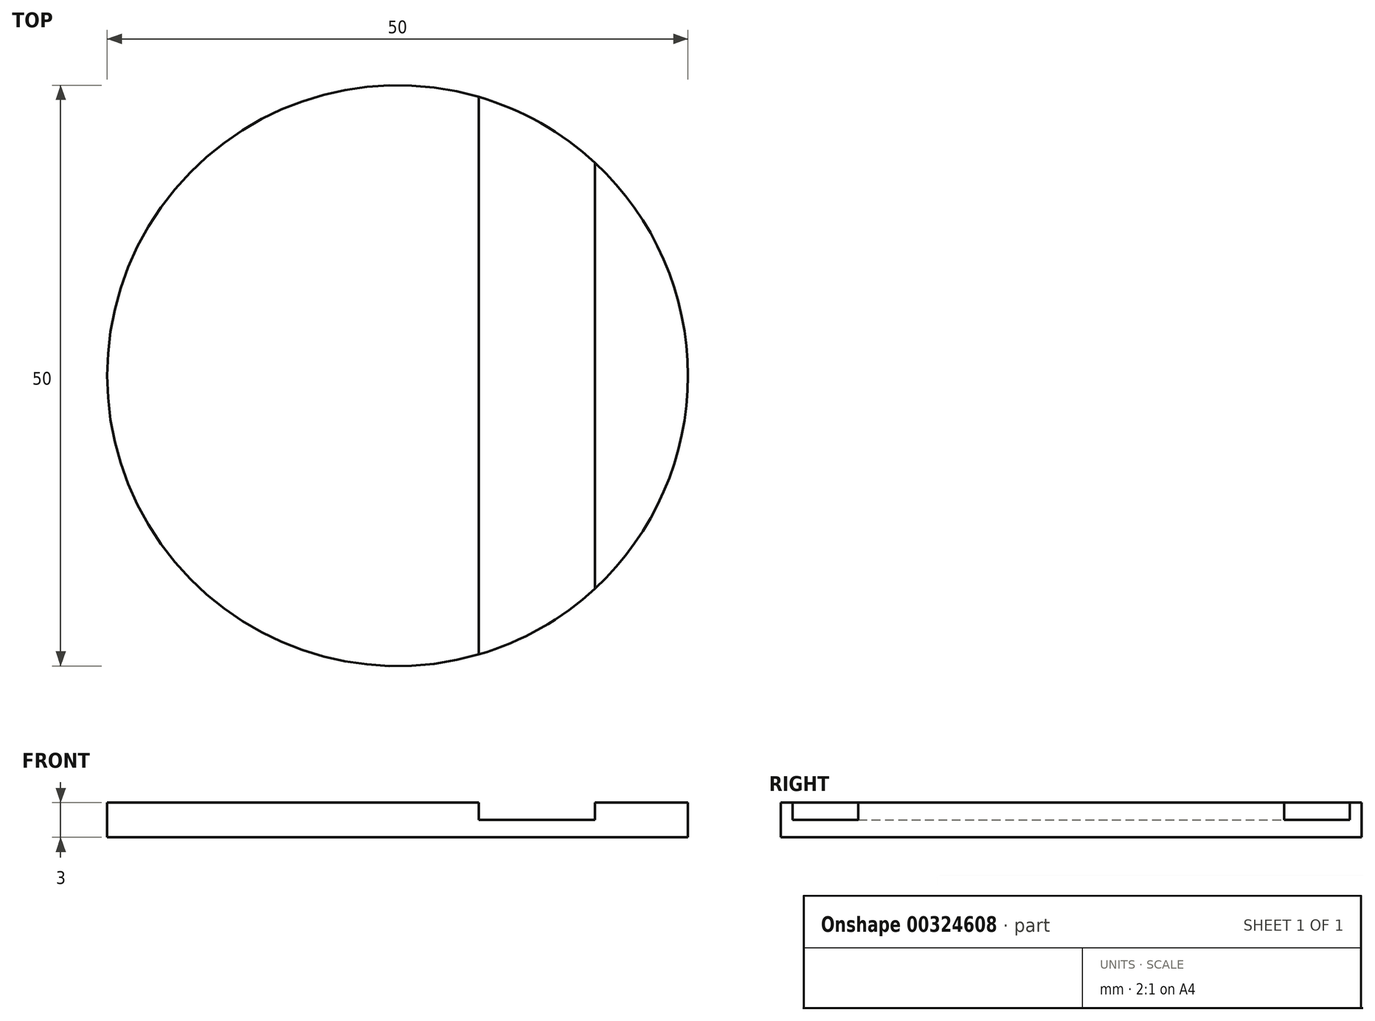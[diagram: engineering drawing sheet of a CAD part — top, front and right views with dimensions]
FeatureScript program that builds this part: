
annotation { "Feature Type Name" : "Feature", "Feature Type Description" : "" }
export const myFeature = defineFeature(function(context is Context, id is Id, definition is map)
    precondition{}
    {
        {
            var Q0;
            Q0=qCreatedBy(makeId("Top.planeOp"),FACE);
            var sketch = newSketch(context, id + "F0", { "sketchPlane" : qUnion([Q0])});
            skCircle(sketch, "E0", {"center": v(0, 0) * mm, "radius": 25 * mm});
            skLineSegment(sketch, "E1", {"start": v(17, -18.33) * mm, "end": v(17, 18.33) * mm});
            skLineSegment(sketch, "E2", {"start": v(7, 24) * mm, "end": v(7, -24) * mm});
            skSolve(sketch);
        }
        {
            var Q0;
            {var subQ0=sQuery(id+"F0.wireOp",EDGE,"E2");Q0=makeQuery(id+"F0.imprint","IMPRINT",FACE,{"disambiguationData":[TD([[makeQuery(id+"F0.imprint","IMPRINT",EDGE,{"derivedFrom":subQ0}),-1.0]])]});}
            var Q1;
            {var subQ0=sQuery(id+"F0.wireOp",EDGE,"E1");Q1=makeQuery(id+"F0.imprint","IMPRINT",FACE,{"disambiguationData":[TD([[makeQuery(id+"F0.imprint","IMPRINT",EDGE,{"derivedFrom":subQ0}),1.0]])]});}
            var Q2;
            {var subQ0=sQuery(id+"F0.wireOp",EDGE,"E1");Q2=makeQuery(id+"F0.imprint","IMPRINT",FACE,{"disambiguationData":[TD([[makeQuery(id+"F0.imprint","IMPRINT",EDGE,{"derivedFrom":subQ0}),-1.0]])]});}
            extrude(context, id + "F1", {"entities" : qUnion([Q0, Q1, Q2]), "oppositeDirection" : true, "depth" : 1.5 * mm, "offsetDistance" : 25 * mm});
        }
        {
            var Q0;
            {var subQ0=sQuery(id+"F0.wireOp",EDGE,"E1");Q0=makeQuery(id+"F0.imprint","IMPRINT",FACE,{"disambiguationData":[TD([[makeQuery(id+"F0.imprint","IMPRINT",EDGE,{"derivedFrom":subQ0}),-1.0]])]});}
            var Q1;
            {var subQ0=sQuery(id+"F0.wireOp",EDGE,"E2");Q1=makeQuery(id+"F0.imprint","IMPRINT",FACE,{"disambiguationData":[TD([[makeQuery(id+"F0.imprint","IMPRINT",EDGE,{"derivedFrom":subQ0}),-1.0]])]});}
            extrude(context, id + "F2", {"entities" : qUnion([Q0, Q1]), "operationType" : NewBodyOperationType.ADD, "depth" : 1.5 * mm, "offsetDistance" : 25 * mm});
        }
    });
